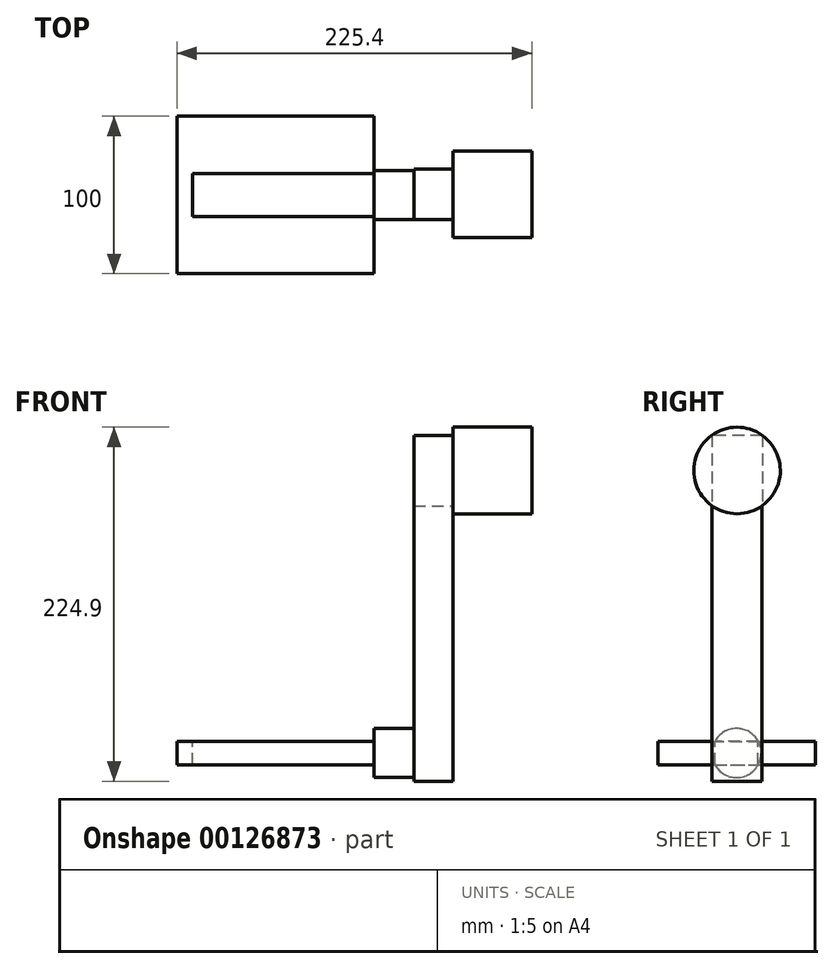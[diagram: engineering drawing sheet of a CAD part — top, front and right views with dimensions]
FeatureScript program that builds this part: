
annotation { "Feature Type Name" : "Feature", "Feature Type Description" : "" }
export const myFeature = defineFeature(function(context is Context, id is Id, definition is map)
    precondition{}
    {
        {
            var Q0;
            Q0=qCreatedBy(makeId("Right.planeOp"),FACE);
            var sketch = newSketch(context, id + "F0", { "sketchPlane" : qUnion([Q0])});
            skCircle(sketch, "E0", {"center": v(20.38, 26.13) * mm, "radius": 27.5 * mm});
            skSolve(sketch);
        }
        {
            var Q0;
            Q0=makeQuery(id+"F0.imprint","IMPRINT",FACE,{"disambiguationData":[TD([[makeQuery(id+"F0.imprint","IMPRINT",EDGE,{"derivedFrom":sQuery(id+"F0.wireOp",EDGE,"E0")}),1.0]])]});
            extrude(context, id + "F1", {"entities" : qUnion([Q0]), "depth" : 50 * mm});
        }
        {
            var Q0;
            Q0=makeQuery(id+"F1.opExtrude","CAP_FACE",FACE,{"disambiguationData":[OSD([sQuery(id+"F0.wireOp",EDGE,"E0")])],"isStart":true});
            var sketch = newSketch(context, id + "F2", { "sketchPlane" : qUnion([Q0])});
            skLineSegment(sketch, "E1.bottom", {"start": v(-36.45, 48.45) * mm, "end": v(-4.43, 48.45) * mm});
            skLineSegment(sketch, "E1.top", {"start": v(-36.45, 3.73) * mm, "end": v(-4.43, 3.73) * mm});
            skLineSegment(sketch, "E1.left", {"start": v(-36.45, 48.45) * mm, "end": v(-36.45, 3.73) * mm});
            skLineSegment(sketch, "E1.right", {"start": v(-4.43, 48.45) * mm, "end": v(-4.43, 3.73) * mm});
            skSolve(sketch);
        }
        {
            var Q0;
            {var subQ0=sQuery(id+"F2.wireOp",EDGE,"E1.left");var subQ1=sQuery(id+"F2.wireOp",EDGE,"E1.top");var subQ2=makeQuery(id+"F2.imprint","INTERSECT",VERTEX,{"derivedFrom":[subQ1,subQ0]});Q0=makeQuery(id+"F2.imprint","IMPRINT",FACE,{"disambiguationData":[TD([[makeQuery(id+"F2.imprint","IMPRINT",EDGE,{"disambiguationData":[TD([[subQ2,-1.0]])],"derivedFrom":subQ1}),1.0]])]});}
            var Q1;
            {var subQ2=sQuery(id+"F2.wireOp",EDGE,"E1.bottom");Q1=makeQuery(id+"F2.imprint","IMPRINT",FACE,{"disambiguationData":[TD([[makeQuery(id+"F2.imprint","IMPRINT",EDGE,{"derivedFrom":subQ2}),-1.0]])]});}
            extrude(context, id + "F3", {"entities" : qUnion([Q0, Q1]), "operationType" : NewBodyOperationType.ADD, "depth" : 25 * mm});
        }
        {
            var Q0;
            Q0=makeQuery(id+"F3.opExtrude","SWEPT_FACE",FACE,{"disambiguationData":[OSD([sQuery(id+"F2.wireOp",EDGE,"E1.top")])]});
            var sketch = newSketch(context, id + "F4", { "sketchPlane" : qUnion([Q0])});
            skLineSegment(sketch, "E2.bottom", {"start": v(-25, -4.43) * mm, "end": v(0, -4.43) * mm});
            skLineSegment(sketch, "E2.top", {"start": v(-25, -36.33) * mm, "end": v(0, -36.33) * mm});
            skLineSegment(sketch, "E2.left", {"start": v(-25, -4.43) * mm, "end": v(-25, -36.33) * mm});
            skLineSegment(sketch, "E2.right", {"start": v(0, -4.43) * mm, "end": v(0, -36.33) * mm});
            skSolve(sketch);
        }
        {
            var Q0;
            Q0=makeQuery(id+"F4.imprint","IMPRINT",FACE,{"disambiguationData":[TD([[makeQuery(id+"F4.imprint","IMPRINT",EDGE,{"derivedFrom":sQuery(id+"F4.wireOp",EDGE,"E2.bottom")}),-1.0]])]});
            extrude(context, id + "F5", {"entities" : qUnion([Q0]), "operationType" : NewBodyOperationType.ADD, "depth" : 175 * mm});
        }
        {
            var Q0;
            Q0=makeQuery(id+"F5.boolean.opBoolean","MERGE",FACE,{"derivedFrom":[makeQuery(id+"F3.opExtrude","CAP_FACE",FACE,{"disambiguationData":[OSD([sQuery(id+"F2.wireOp",EDGE,"E1.bottom"),sQuery(id+"F2.wireOp",EDGE,"E1.top"),sQuery(id+"F2.wireOp",EDGE,"E1.left"),sQuery(id+"F2.wireOp",EDGE,"E1.right")])],"isStart":false}),makeQuery(id+"F5.opExtrude","SWEPT_FACE",FACE,{"disambiguationData":[OSD([sQuery(id+"F4.wireOp",EDGE,"E2.left")])]})]});
            var sketch = newSketch(context, id + "F6", { "sketchPlane" : qUnion([Q0])});
            skCircle(sketch, "E3", {"center": v(-20.06, -153.35) * mm, "radius": 15.62 * mm});
            skSolve(sketch);
        }
        {
            var Q0;
            Q0 = qSketchRegion(id + "F6", true);
            var Q1;
            Q1=makeQuery(id+"F6.imprint","IMPRINT",FACE,{"disambiguationData":[TD([[makeQuery(id+"F6.imprint","IMPRINT",EDGE,{"derivedFrom":sQuery(id+"F6.wireOp",EDGE,"E3")}),1.0]])]});
            extrude(context, id + "F7", {"entities" : qUnion([Q0, Q1]), "operationType" : NewBodyOperationType.ADD, "depth" : 25.4 * mm});
        }
        {
            var Q0;
            Q0=makeQuery(id+"F7.opExtrude","CAP_FACE",FACE,{"disambiguationData":[OSD([sQuery(id+"F6.wireOp",EDGE,"E3")])],"isStart":false});
            var sketch = newSketch(context, id + "F8", { "sketchPlane" : qUnion([Q0])});
            skPoint(sketch, "E4", {"position": v(-20.06, -153.35) * mm});
            skLineSegment(sketch, "E5.bottom", {"start": v(29.94, -145.85) * mm, "end": v(-70.06, -145.85) * mm});
            skLineSegment(sketch, "E5.top", {"start": v(29.94, -160.85) * mm, "end": v(-70.06, -160.85) * mm});
            skLineSegment(sketch, "E5.left", {"start": v(29.94, -145.85) * mm, "end": v(29.94, -160.85) * mm});
            skLineSegment(sketch, "E5.right", {"start": v(-70.06, -145.85) * mm, "end": v(-70.06, -160.85) * mm});
            skSolve(sketch);
        }
        {
            var Q0;
            {var subQ0=sQuery(id+"F8.wireOp",EDGE,"E5.left");Q0=makeQuery(id+"F8.imprint","IMPRINT",FACE,{"disambiguationData":[TD([[makeQuery(id+"F8.imprint","IMPRINT",EDGE,{"derivedFrom":subQ0}),-1.0]])]});}
            var Q1;
            {var subQ0=sQuery(id+"F8.wireOp",EDGE,"E5.bottom");var subQ1=makeQuery(id+"F7.opExtrude","CAP_EDGE",EDGE,{"disambiguationData":[OSD([sQuery(id+"F6.wireOp",EDGE,"E3")])],"isStart":false});var subQ2=makeQuery(id+"F8.imprint","INTERSECT",VERTEX,{"disambiguationData":[OD(0.0)],"derivedFrom":[subQ1,subQ0]});Q1=makeQuery(id+"F8.imprint","IMPRINT",FACE,{"disambiguationData":[TD([[makeQuery(id+"F8.imprint","IMPRINT",EDGE,{"disambiguationData":[TD([[subQ2,-1.0]])],"derivedFrom":subQ0}),1.0]])]});}
            var Q2;
            {var subQ0=sQuery(id+"F8.wireOp",EDGE,"E5.right");Q2=makeQuery(id+"F8.imprint","IMPRINT",FACE,{"disambiguationData":[TD([[makeQuery(id+"F8.imprint","IMPRINT",EDGE,{"derivedFrom":subQ0}),1.0]])]});}
            extrude(context, id + "F9", {"entities" : qUnion([Q0, Q1, Q2]), "operationType" : NewBodyOperationType.ADD, "depth" : 125 * mm});
        }
        {
            var Q0;
            Q0=makeQuery(id+"F9.opExtrude","SWEPT_FACE",FACE,{"disambiguationData":[OSD([sQuery(id+"F8.wireOp",EDGE,"E5.bottom")])]});
            var sketch = newSketch(context, id + "F10", { "sketchPlane" : qUnion([Q0])});
            skLineSegment(sketch, "E6.bottom", {"start": v(-50.4, 33.76) * mm, "end": v(-165.5, 33.76) * mm});
            skLineSegment(sketch, "E6.top", {"start": v(-50.4, 6.35) * mm, "end": v(-165.5, 6.35) * mm});
            skLineSegment(sketch, "E6.left", {"start": v(-50.4, 33.76) * mm, "end": v(-50.4, 6.35) * mm});
            skLineSegment(sketch, "E6.right", {"start": v(-165.5, 33.76) * mm, "end": v(-165.5, 6.35) * mm});
            skSolve(sketch);
        }
        {
            var Q0;
            Q0=makeQuery(id+"F10.imprint","IMPRINT",FACE,{"disambiguationData":[TD([[makeQuery(id+"F10.imprint","IMPRINT",EDGE,{"derivedFrom":sQuery(id+"F10.wireOp",EDGE,"E6.bottom")}),1.0]])]});
            extrude(context, id + "F11", {"entities" : qUnion([Q0]), "operationType" : NewBodyOperationType.REMOVE, "oppositeDirection" : true, "depth" : 25.4 * mm});
        }
    });
